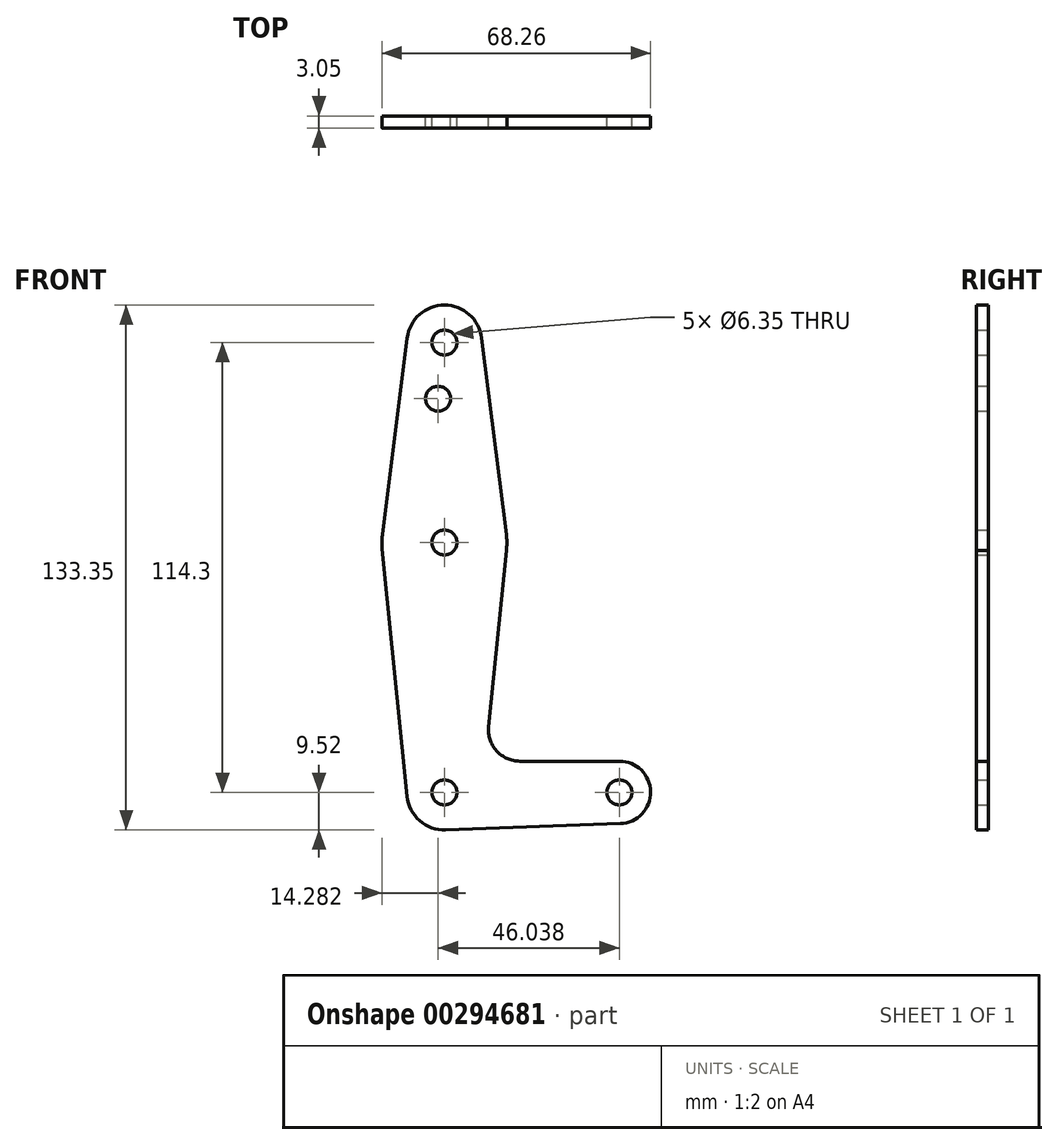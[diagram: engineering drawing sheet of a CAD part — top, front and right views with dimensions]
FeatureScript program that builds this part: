
annotation { "Feature Type Name" : "Feature", "Feature Type Description" : "" }
export const myFeature = defineFeature(function(context is Context, id is Id, definition is map)
    precondition{}
    {
        {
            var Q0;
            Q0=qCreatedBy(makeId("Front.planeOp"),FACE);
            var sketch = newSketch(context, id + "F0", { "sketchPlane" : qUnion([Q0])});
            skCircle(sketch, "E0", {"center": v(0, 0) * mm, "radius": 9.53 * mm});
            skCircle(sketch, "E1", {"center": v(0, 63.5) * mm, "radius": 15.88 * mm});
            skCircle(sketch, "E2", {"center": v(0, 114.3) * mm, "radius": 9.52 * mm});
            skCircle(sketch, "E3", {"center": v(44.45, 0) * mm, "radius": 7.94 * mm});
            skLineSegment(sketch, "E4", {"start": v(0, 114.3) * mm, "end": v(0, 0) * mm, "construction": true});
            skLineSegment(sketch, "E5", {"start": v(0, 0) * mm, "end": v(44.45, 0) * mm, "construction": true});
            skLineSegment(sketch, "E6", {"start": v(0, 63.5) * mm, "end": v(0, 0) * mm, "construction": true});
            skLineSegment(sketch, "E7", {"start": v(-9.45, 115.5) * mm, "end": v(-15.75, 65.48) * mm});
            skLineSegment(sketch, "E8", {"start": v(-15.75, 65.48) * mm, "end": v(-15.75, 61.52) * mm});
            skLineSegment(sketch, "E9", {"start": v(9.45, 115.5) * mm, "end": v(15.75, 65.48) * mm});
            skLineSegment(sketch, "E10", {"start": v(15.75, 65.48) * mm, "end": v(15.75, 61.52) * mm});
            skLineSegment(sketch, "E11", {"start": v(15.75, 61.52) * mm, "end": v(11.25, 16.68) * mm});
            skLineSegment(sketch, "E12", {"start": v(44.73, -7.93) * mm, "end": v(0, -9.53) * mm});
            skLineSegment(sketch, "E13", {"start": v(44.45, 7.94) * mm, "end": v(19.16, 7.94) * mm});
            skCircle(sketch, "E14", {"center": v(0, 114.3) * mm, "radius": 3.18 * mm});
            skCircle(sketch, "E15", {"center": v(0, 63.5) * mm, "radius": 3.18 * mm});
            skCircle(sketch, "E16", {"center": v(0, 0) * mm, "radius": 3.18 * mm});
            skCircle(sketch, "E17", {"center": v(44.45, 0) * mm, "radius": 3.18 * mm});
            skLineSegment(sketch, "E18", {"start": v(-15.8, 61.91) * mm, "end": v(-9.48, -0.95) * mm});
            skPoint(sketch, "E19.newPointA", {"position": v(9.57, 0) * mm});
            skArc(sketch, "E19.filletArc", {"start": v(11.25, 16.68) * mm, "mid": v(13.26, 10.55) * mm, "end": v(19.16, 7.94) * mm});
            skCircle(sketch, "E20", {"center": v(-1.59, 100.03) * mm, "radius": 3.18 * mm});
            skSolve(sketch);
        }
        {
            var Q0;
            Q0 = qSketchRegion(id + "F0", true);
            extrude(context, id + "F1", {"entities" : qUnion([Q0]), "depth" : 3.05 * mm});
        }
    });
